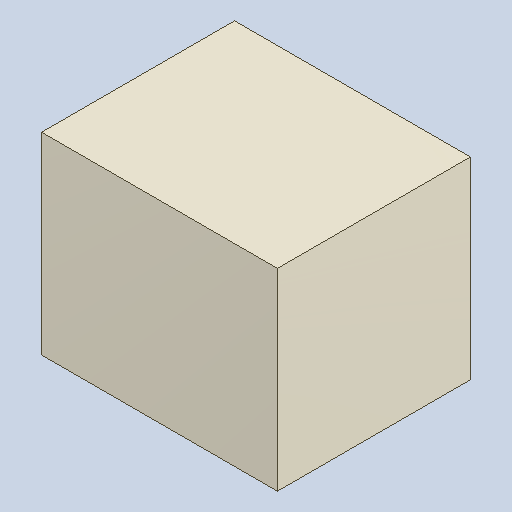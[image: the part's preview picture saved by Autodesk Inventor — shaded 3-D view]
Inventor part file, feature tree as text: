
AUTODESK INVENTOR PART (.ipt)
format: ipt  version: 2023.4 (Build 274418000, 418)  size: 81,920 bytes
history: native  units: mm
features: extrude x1
ambient origin geometry x8: Origin, YZ Plane, XZ Plane, XY Plane, X Axis, Y Axis, Z Axis, Center Point
bodies: Solid1 (feature_tree)
feature tree (1):
  extrude  "Extruded_21"  [1 undecoded]
note: 1 required parameter value undecoded (feature->parameter linkage not recoverable at this tier; creation-order binding heuristic only, values carry confidence <= 0.55)
